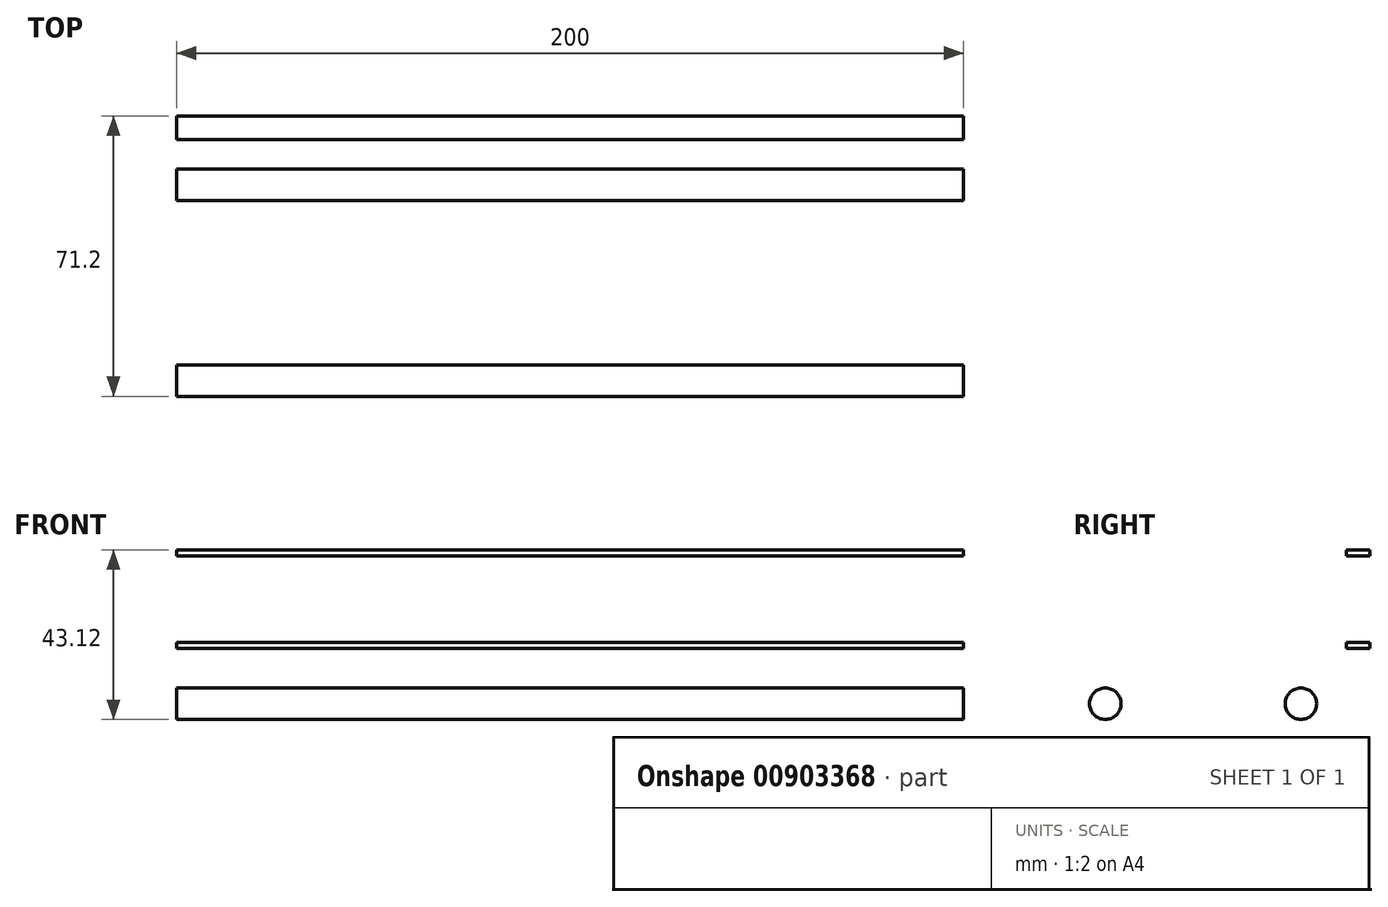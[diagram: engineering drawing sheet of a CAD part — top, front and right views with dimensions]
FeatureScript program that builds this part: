
annotation { "Feature Type Name" : "Feature", "Feature Type Description" : "" }
export const myFeature = defineFeature(function(context is Context, id is Id, definition is map)
    precondition{}
    {
        {
            var Q0;
            Q0=qCreatedBy(makeId("Right.planeOp"),FACE);
            var sketch = newSketch(context, id + "F0", { "sketchPlane" : qUnion([Q0])});
            skCircle(sketch, "E0", {"center": v(-24.85, 0) * mm, "radius": 4 * mm});
            skLineSegment(sketch, "E1", {"start": v(0, 0) * mm, "end": v(0, 68.8) * mm, "construction": true});
            skCircle(sketch, "E2.MirrorC", {"center": v(24.85, 0) * mm, "radius": 4 * mm});
            skPoint(sketch, "E3", {"position": v(-20.85, 0) * mm});
            skPoint(sketch, "E4", {"position": v(20.85, 0) * mm});
            skLineSegment(sketch, "E5.bottom", {"start": v(36.35, 15.56) * mm, "end": v(42.35, 15.56) * mm});
            skLineSegment(sketch, "E5.top", {"start": v(36.35, 14) * mm, "end": v(42.35, 14) * mm});
            skLineSegment(sketch, "E5.left", {"start": v(36.35, 15.56) * mm, "end": v(36.35, 14) * mm});
            skLineSegment(sketch, "E5.right", {"start": v(42.35, 15.56) * mm, "end": v(42.35, 14) * mm});
            skLineSegment(sketch, "E6.bottom", {"start": v(36.35, 39.12) * mm, "end": v(42.35, 39.12) * mm});
            skLineSegment(sketch, "E6.top", {"start": v(36.35, 37.56) * mm, "end": v(42.35, 37.56) * mm});
            skLineSegment(sketch, "E6.left", {"start": v(36.35, 39.12) * mm, "end": v(36.35, 37.56) * mm});
            skLineSegment(sketch, "E6.right", {"start": v(42.35, 39.12) * mm, "end": v(42.35, 37.56) * mm});
            skLineSegment(sketch, "E7", {"start": v(24.85, 0) * mm, "end": v(24.85, 4) * mm, "construction": true});
            skSolve(sketch);
        }
        {
            var Q0;
            Q0 = qSketchRegion(id + "F0", true);
            extrude(context, id + "F1", {"entities" : qUnion([Q0]), "endBound" : BoundingType.SYMMETRIC, "depth" : 200 * mm, "offsetDistance" : 25 * mm});
        }
    });
